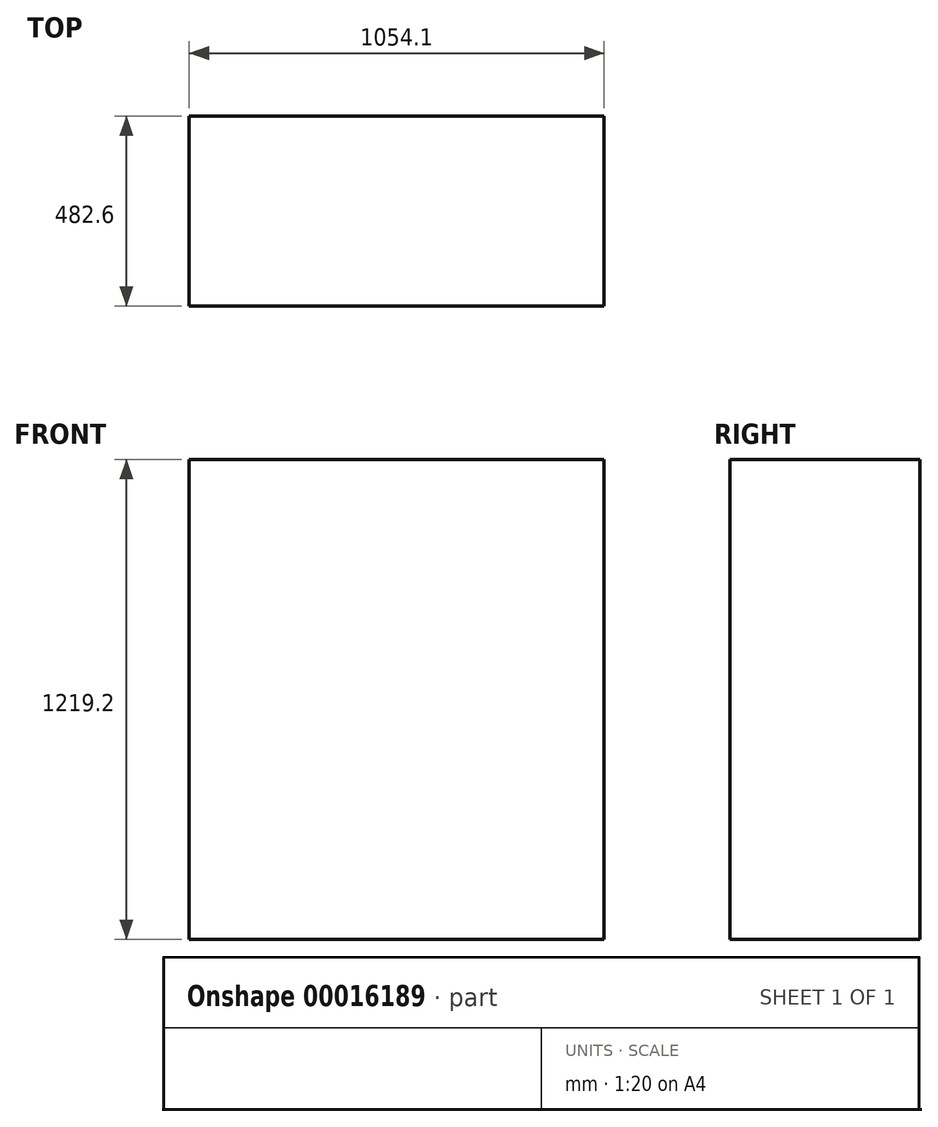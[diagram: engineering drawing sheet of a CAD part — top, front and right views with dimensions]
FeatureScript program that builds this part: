
annotation { "Feature Type Name" : "Feature", "Feature Type Description" : "" }
export const myFeature = defineFeature(function(context is Context, id is Id, definition is map)
    precondition{}
    {
        {
            var Q0;
            Q0=qCreatedBy(makeId("Top.planeOp"),FACE);
            var sketch = newSketch(context, id + "F0", { "sketchPlane" : qUnion([Q0])});
            skLineSegment(sketch, "E0.rect.bottom", {"start": v(527.05, 241.3) * mm, "end": v(-527.05, 241.3) * mm});
            skLineSegment(sketch, "E0.rect.top", {"start": v(527.05, -241.3) * mm, "end": v(-527.05, -241.3) * mm});
            skLineSegment(sketch, "E0.rect.left", {"start": v(527.05, 241.3) * mm, "end": v(527.05, -241.3) * mm});
            skLineSegment(sketch, "E0.rect.right", {"start": v(-527.05, 241.3) * mm, "end": v(-527.05, -241.3) * mm});
            skPoint(sketch, "E0.rect.middle", {"position": v(0, 0) * mm});
            skSolve(sketch);
        }
        {
            var Q0;
            Q0 = qSketchRegion(id + "F0", true);
            extrude(context, id + "F1", {"entities" : qUnion([Q0]), "depth" : 4 * 304.8 * mm});
        }
    });
